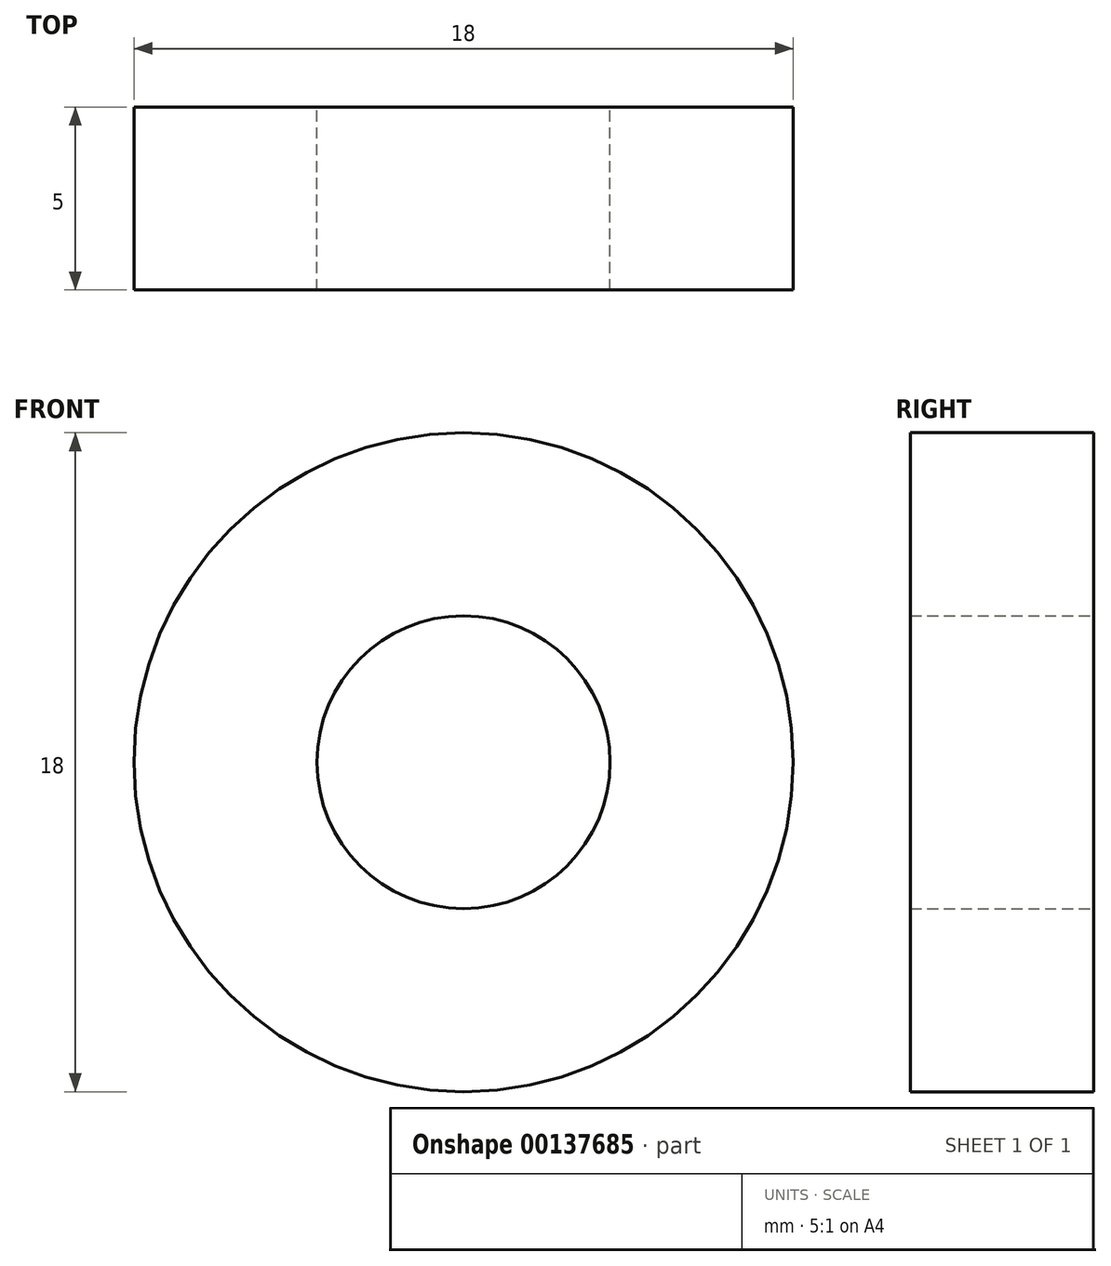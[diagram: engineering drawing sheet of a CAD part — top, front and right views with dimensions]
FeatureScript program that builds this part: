
annotation { "Feature Type Name" : "Feature", "Feature Type Description" : "" }
export const myFeature = defineFeature(function(context is Context, id is Id, definition is map)
    precondition{}
    {
        {
            var Q0;
            Q0=qCreatedBy(makeId("Front.planeOp"),FACE);
            var sketch = newSketch(context, id + "F0", { "sketchPlane" : qUnion([Q0])});
            skCircle(sketch, "E0", {"center": v(0, 0) * mm, "radius": 4 * mm});
            skCircle(sketch, "E1", {"center": v(0, 0) * mm, "radius": 9 * mm});
            skSolve(sketch);
        }
        {
            var Q0;
            Q0=makeQuery(id+"F0.imprint","IMPRINT",FACE,{"disambiguationData":[TD([[makeQuery(id+"F0.imprint","IMPRINT",EDGE,{"derivedFrom":sQuery(id+"F0.wireOp",EDGE,"E0")}),-1.0]])]});
            extrude(context, id + "F1", {"entities" : qUnion([Q0]), "depth" : 5 * mm, "offsetDistance" : 25 * mm});
        }
    });
